# Revit family: Sanitary_Waste-Bins_Hags_Trash-paper
name_source: partatom
category: Furniture
revit_build: Autodesk Revit 2018 (Build: 20190510_1515(x64)
units: mm (PartAtom-declared; Revit-internal decimal feet)

## family parameters
Always vertical = Yes
Cut with Voids When Loaded = No
OmniClass Number = 23.21.17.11
OmniClass Title = Interior Waste Bins
Room Calculation Point = No
Shared = No
Work Plane-Based = No

## types (5) — shared parameters
BIMobject category = Waste Bins
Description = Rosenlund Recycle Bin
Edition number = 1
IFC Classification = Object
Manufacturer = Hags
Manufacturer name = HAGS
OmniClass Code = 23-21 17 11
OmniClass Description = Interior Waste Bins
Product Guid = 0105f79f-af7f-46d7-8fc4-744b74798856
Product SKU = Trash_paper
Product data url = https://bimobject.com
Product name = Rosenlund Recycle Bin
Product url = https://hags.se
QR code = https://bimobject.com
Sign material = Hags - Steel - Powder coated - Light gray
URL = https://www.hags.com
Uniclass 1.4 Code = JN
Uniclass 1.4 Description = Furniture/Equipment

## per-type parameters (varying)
| type | Construction material | Model |
| 8080288 Galvanized | Hags - Steel - Galvanized | 8080288 |
| 8080295 Red | Hags - Steel - Powder coated - Red | 8080295 |
| 8080296 Green | Hags - Steel - Powder coated - Green | 8080296 |
| 8080297 Blue | Hags - Steel - Powder coated - Blue | 8080297 |
| 8080294 Gray | Hags - Steel - Powder coated - Gray | 8080294 |

## geometry (parser evidence)
native form markers: Sweep x3
no freeform markers — native parametric forms only
